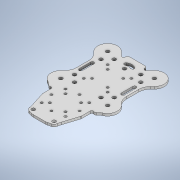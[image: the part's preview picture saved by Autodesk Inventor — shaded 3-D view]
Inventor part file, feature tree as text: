
AUTODESK INVENTOR PART (.ipt)
format: ipt  version: 2020 (Build 240168000, 168)  size: 264,192 bytes
history: native  units: mm
features: extrude x1, sketch x1
ambient origin geometry x8: Origin, YZ Plane, XZ Plane, XY Plane, X Axis, Y Axis, Z Axis, Center Point
bodies: Solid1 (feature_tree)
feature tree (2):
  extrude  "Extrusion1"  [1 undecoded]
  sketch  "Sketch1"  dims[d0=3.0mm d1=0.0mm]
note: 1 required parameter value undecoded (feature->parameter linkage not recoverable at this tier; creation-order binding heuristic only, values carry confidence <= 0.55)
